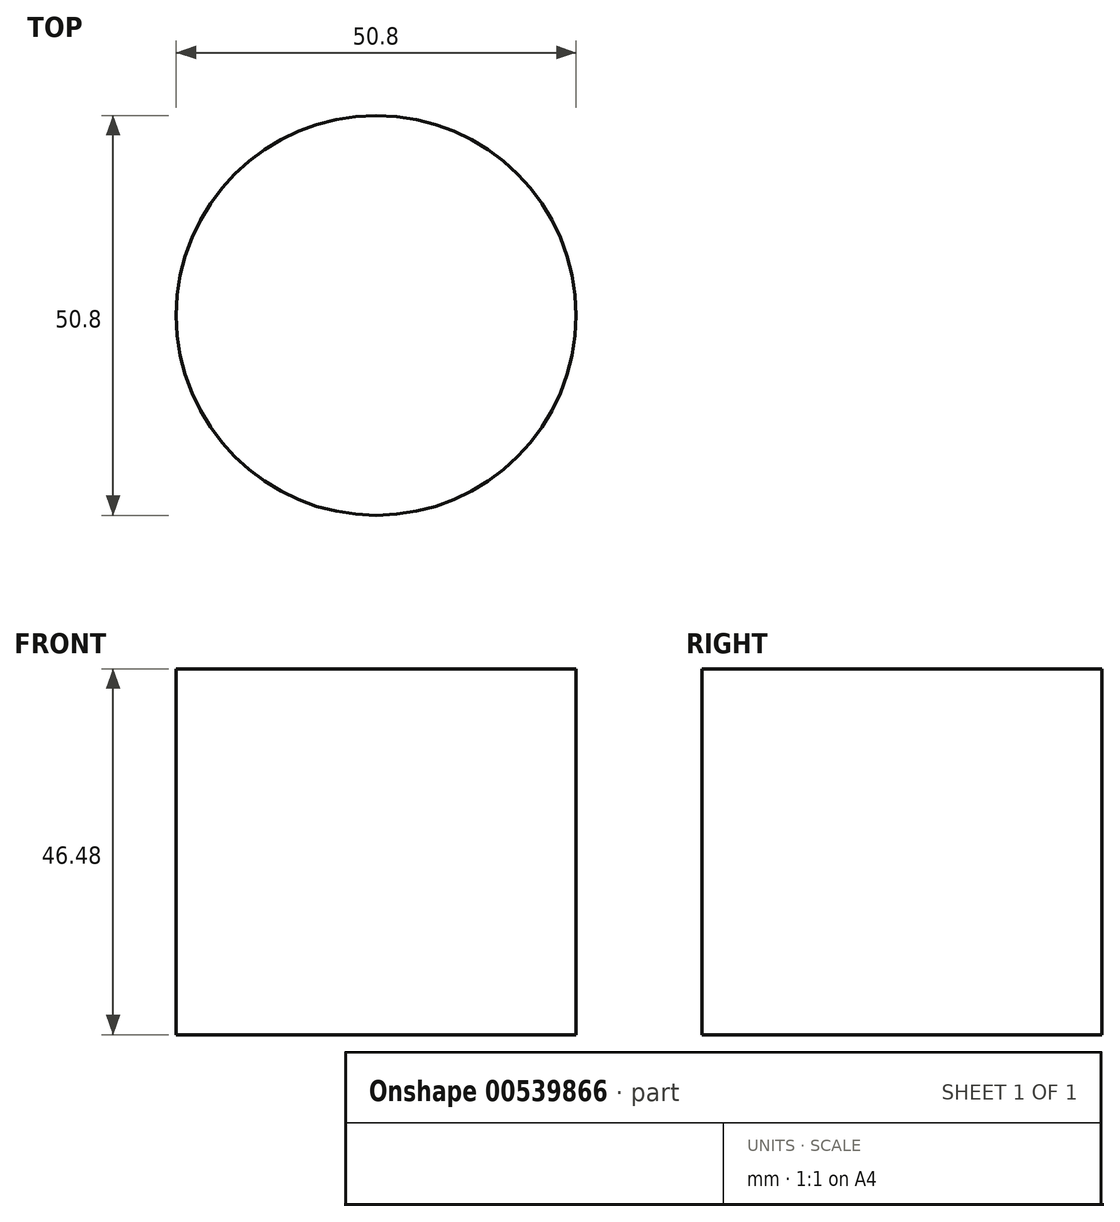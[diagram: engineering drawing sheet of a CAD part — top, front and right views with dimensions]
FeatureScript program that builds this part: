
annotation { "Feature Type Name" : "Feature", "Feature Type Description" : "" }
export const myFeature = defineFeature(function(context is Context, id is Id, definition is map)
    precondition{}
    {
        {
            var Q0;
            Q0=qCreatedBy(makeId("Top.planeOp"),FACE);
            var sketch = newSketch(context, id + "F0", { "sketchPlane" : qUnion([Q0])});
            skCircle(sketch, "E0", {"center": v(0, 0) * mm, "radius": 25.4 * mm});
            skSolve(sketch);
        }
        {
            var Q0;
            Q0=makeQuery(id+"F0.imprint","IMPRINT",FACE,{"disambiguationData":[TD([[makeQuery(id+"F0.imprint","IMPRINT",EDGE,{"derivedFrom":sQuery(id+"F0.wireOp",EDGE,"E0")}),1.0]])]});
            extrude(context, id + "F1", {"entities" : qUnion([Q0]), "depth" : 46.48 * mm, "offsetDistance" : 25.4 * mm});
        }
    });
